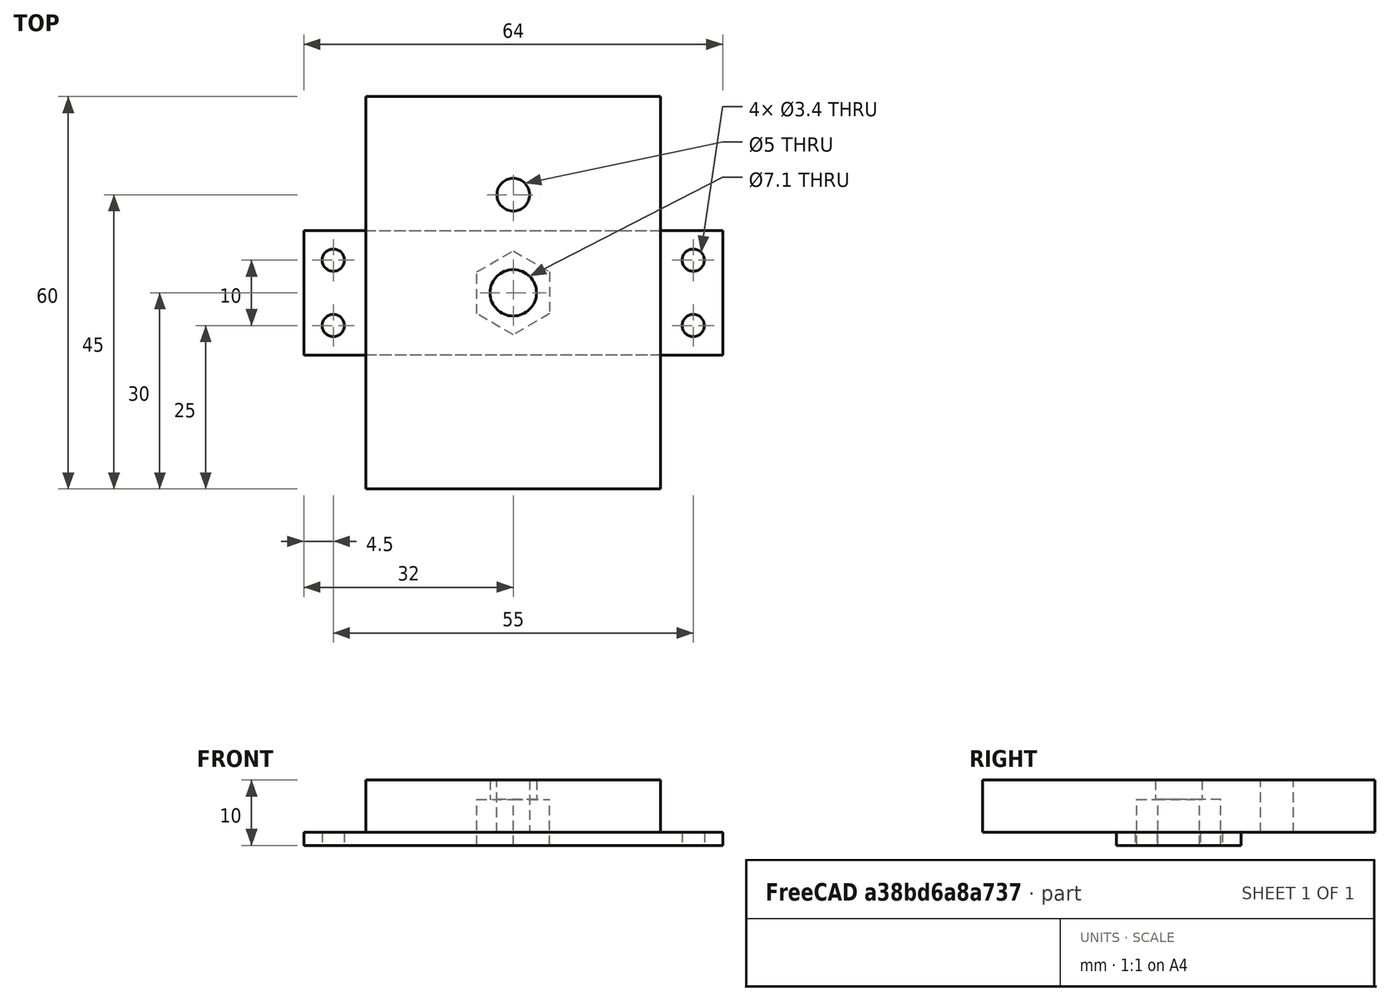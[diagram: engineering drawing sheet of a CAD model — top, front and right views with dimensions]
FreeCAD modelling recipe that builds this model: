
FCSTD DOCUMENT  (FreeCAD 0.21R33668 +26 (Git))
Label: Tripod_Connector
License: All rights reserved
LicenseURL: https://en.wikipedia.org/wiki/All_rights_reserved
objects: Sketcher::SketchObject×6, PartDesign::Pad×2, PartDesign::Hole×2, PartDesign::Pocket×2, Spreadsheet::Sheet×1, PartDesign::Body×1, Mesh::Feature×1
note: 19 computed .brp shape members not serialized (recipe doc carries the construction recipe); baked Part::Feature solids carry a one-line shape summary decoded from their .brp
EXTERNAL_REF file=Casing2.FCStd obj=Spreadsheet

FEATURE [Spreadsheet::Sheet] Spreadsheet
  cells = B2='interface_width; C2(interface_width)==<<Casing2>>#Spreadsheet.interface_width; E2='plate_width; F2(plate_width)==45 mm; H2='hole_rad; I2(hole_rad)==2.5 mm; B3='interface_height; C3(interface_height)==<<Casing2>>#Spreadsheet.beams_width * 2; E3='plate_height; F3(plate_height)==60 mm; H3='dist; I3(dist)==15 mm; B4='interface_depth; C4(interface_depth)==<<Casing2>>#Spreadsheet.walls_thickness; E4='plate_depth; F4(plate_depth)==8 mm; H4='nut_depth; I4(nut_depth)==interface_depth + plate_depth - 3 mm; B5='screw_radius; C5(screw_radius)==<<Casing2>>#Spreadsheet.screw_radius
FEATURE [Sketcher::SketchObject] Sketch
  FullyConstrained = true
  MapMode = 5
  Support = -> [XY_Plane]
  expr: Constraints[10] = Spreadsheet.interface_height - 1 mm
  expr: Constraints[9] = Spreadsheet.interface_width - 1 mm
  sketch-geometry (4):
    g0: LineSegment StartX=-32 StartY=9.5 StartZ=0 EndX=32 EndY=9.5 EndZ=0
    g1: LineSegment StartX=32 StartY=9.5 StartZ=0 EndX=32 EndY=-9.5 EndZ=0
    g2: LineSegment StartX=32 StartY=-9.5 StartZ=0 EndX=-32 EndY=-9.5 EndZ=0
    g3: LineSegment StartX=-32 StartY=-9.5 StartZ=0 EndX=-32 EndY=9.5 EndZ=0
  constraints (11):
    c: Coincident(g0,g1)
    c: Coincident(g1,g2)
    c: Coincident(g2,g3)
    c: Coincident(g3,g0)
    c: Horizontal(g0)
    c: Horizontal(g2)
    c: Vertical(g1)
    c: Vertical(g3)
    c: Symmetric(g0,g2,g-1)
    c: DistanceX(g0,g0) = 64
    c: DistanceY(g3,g3) = 19
FEATURE [PartDesign::Pad] Pad
  Direction = (0,0,1)
  Length = 2
  Length2 = 10
  Profile = -> Sketch
  ReferenceAxis = -> Sketch [N_Axis]
  Type = 0
  expr: Length = Spreadsheet.interface_depth
FEATURE [Sketcher::SketchObject] Sketch001
  FullyConstrained = true
  MapMode = 5
  Placement = pos=(0,0,2) rot=(0,0,1;0rad)
  Support = -> [Pad]
  expr: Constraints[10] = Spreadsheet.interface_height
  expr: Constraints[11] = Spreadsheet.interface_height / 4
  expr: Constraints[12] = Spreadsheet.interface_height / 4
  expr: Constraints[13] = Spreadsheet.interface_height / 4
  expr: Constraints[14] = Spreadsheet.interface_height / 4
  expr: Constraints[15] = Spreadsheet.interface_height / 4
  expr: Constraints[16] = Spreadsheet.interface_height / 4
  expr: Constraints[17] = Spreadsheet.interface_height / 4
  expr: Constraints[18] = Spreadsheet.interface_height / 4
  expr: Constraints[19] = Spreadsheet.screw_radius
  expr: Constraints[20] = Spreadsheet.screw_radius
  expr: Constraints[21] = Spreadsheet.screw_radius
  expr: Constraints[22] = Spreadsheet.screw_radius
  expr: Constraints[9] = Spreadsheet.interface_width
  sketch-geometry (8):
    g0: LineSegment StartX=-32.5 StartY=10 StartZ=0 EndX=32.5 EndY=10 EndZ=0
    g1: LineSegment StartX=32.5 StartY=10 StartZ=0 EndX=32.5 EndY=-10 EndZ=0
    g2: LineSegment StartX=32.5 StartY=-10 StartZ=0 EndX=-32.5 EndY=-10 EndZ=0
    g3: LineSegment StartX=-32.5 StartY=-10 StartZ=0 EndX=-32.5 EndY=10 EndZ=0
    g4: Circle CenterX=-27.5 CenterY=5 CenterZ=0 NormalX=0 NormalY=0 NormalZ=1 AngleXU=0 Radius=1.5
    g5: Circle CenterX=-27.5 CenterY=-5 CenterZ=0 NormalX=0 NormalY=0 NormalZ=1 AngleXU=0 Radius=1.5
    g6: Circle CenterX=27.5 CenterY=5 CenterZ=0 NormalX=0 NormalY=0 NormalZ=1 AngleXU=0 Radius=1.5
    g7: Circle CenterX=27.5 CenterY=-5 CenterZ=0 NormalX=0 NormalY=0 NormalZ=1 AngleXU=0 Radius=1.5
  constraints (23):
    c: Coincident(g0,g1)
    c: Coincident(g1,g2)
    c: Coincident(g2,g3)
    c: Coincident(g3,g0)
    c: Horizontal(g0)
    c: Horizontal(g2)
    c: Vertical(g1)
    c: Vertical(g3)
    c: Symmetric(g0,g2,g-1)
    c: DistanceX(g0,g0) = 65
    c: DistanceY(g3,g3) = 20
    c: DistanceX(g0,g4) = 5
    c: DistanceX(g6,g0) = 5
    c: DistanceX(g7,g1) = 5
    c: DistanceX(g2,g5) = 5
    c: DistanceY(g4,g0) = 5
    c: DistanceY(g6,g0) = 5
    c: DistanceY(g1,g7) = 5
    c: DistanceY(g2,g5) = 5
    c: Radius(g6) = 1.5
    c: Radius(g7) = 1.5
    c: Radius(g4) = 1.5
    c: Radius(g5) = 1.5
FEATURE [PartDesign::Hole] Hole
  BaseFeature = -> Pad
  CustomThreadClearance = 0
  Depth = 134.917
  DepthType = 1
  Diameter = 3.4
  DrillForDepth = false
  DrillPoint = 1
  DrillPointAngle = 118
  HoleCutCountersinkAngle = 90
  HoleCutCustomValues = false
  HoleCutDepth = 0
  HoleCutDiameter = 6.1
  HoleCutType = 0
  ModelThread = false
  Profile = -> Sketch001
  Tapered = false
  TaperedAngle = 90
  ThreadClass = 0
  ThreadDepth = 134.917
  ThreadDepthType = 0
  ThreadDirection = 0
  ThreadFit = 0
  ThreadSize = 9
  ThreadType = 1
  Threaded = false
  UseCustomThreadClearance = false
FEATURE [Sketcher::SketchObject] Sketch002
  FullyConstrained = true
  MapMode = 5
  Placement = pos=(0,0,2) rot=(0,0,1;0rad)
  Support = -> [Hole]
  expr: Constraints[10] = Spreadsheet.plate_height
  expr: Constraints[9] = Spreadsheet.plate_width
  sketch-geometry (4):
    g0: LineSegment StartX=-22.5 StartY=30 StartZ=0 EndX=22.5 EndY=30 EndZ=0
    g1: LineSegment StartX=22.5 StartY=30 StartZ=0 EndX=22.5 EndY=-30 EndZ=0
    g2: LineSegment StartX=22.5 StartY=-30 StartZ=0 EndX=-22.5 EndY=-30 EndZ=0
    g3: LineSegment StartX=-22.5 StartY=-30 StartZ=0 EndX=-22.5 EndY=30 EndZ=0
  constraints (11):
    c: Coincident(g0,g1)
    c: Coincident(g1,g2)
    c: Coincident(g2,g3)
    c: Coincident(g3,g0)
    c: Horizontal(g0)
    c: Horizontal(g2)
    c: Vertical(g1)
    c: Vertical(g3)
    c: Symmetric(g0,g2,g-1)
    c: DistanceX(g0,g0) = 45
    c: DistanceY(g3,g3) = 60
FEATURE [PartDesign::Pad] Pad001
  BaseFeature = -> Hole
  Direction = (0,0,1)
  Length = 8
  Length2 = 10
  Profile = -> Sketch002
  ReferenceAxis = -> Sketch002 [N_Axis]
  Type = 0
  expr: Length = Spreadsheet.plate_depth
FEATURE [Sketcher::SketchObject] Sketch003
  FullyConstrained = true
  MapMode = 5
  Placement = pos=(0,0,10) rot=(0,0,1;0rad)
  Support = -> [Pad001]
  expr: Constraints[1] = Spreadsheet.dist
  expr: Constraints[2] = Spreadsheet.hole_rad
  sketch-geometry (1):
    g0: Circle CenterX=0 CenterY=15 CenterZ=0 NormalX=0 NormalY=0 NormalZ=1 AngleXU=0 Radius=2.5
  constraints (3):
    c: PointOnObject(g0,g-2)
    c: DistanceY(g-1,g0) = 15
    c: Radius(g0) = 2.5
FEATURE [PartDesign::Pocket] Pocket
  BaseFeature = -> Pad001
  Direction = (0,0,-1)
  Length = 5
  Length2 = 5
  Profile = -> Sketch003
  ReferenceAxis = -> Sketch003 [N_Axis]
  Type = 1
FEATURE [Sketcher::SketchObject] Sketch004
  FullyConstrained = true
  MapMode = 5
  Placement = pos=(0,0,10) rot=(0,0,1;0rad)
  Support = -> [Pocket]
  sketch-geometry (1):
    g0: Circle CenterX=0 CenterY=0 CenterZ=0 NormalX=0 NormalY=0 NormalZ=1 AngleXU=0 Radius=2.5
  constraints (2):
    c: Coincident(g0,g-1)
    c: Radius(g0) = 2.5
FEATURE [PartDesign::Hole] Hole001
  BaseFeature = -> Pocket
  CustomThreadClearance = 0
  Depth = 178.356
  DepthType = 1
  Diameter = 7.1
  DrillForDepth = false
  DrillPoint = 1
  DrillPointAngle = 118
  HoleCutCountersinkAngle = 90
  HoleCutCustomValues = false
  HoleCutDepth = 0
  HoleCutDiameter = 8.8
  HoleCutType = 0
  ModelThread = false
  Profile = -> Sketch004
  Tapered = false
  TaperedAngle = 90
  ThreadClass = 0
  ThreadDepth = 178.356
  ThreadDepthType = 0
  ThreadDirection = 0
  ThreadFit = 0
  ThreadSize = 9
  ThreadType = 3
  Threaded = false
  UseCustomThreadClearance = false
FEATURE [Sketcher::SketchObject] Sketch005
  FullyConstrained = true
  MapMode = 5
  Placement = pos=(0,0,0) rot=(1,0,0;3.14159rad)
  Support = -> [Hole001]
  sketch-geometry (7):
    g0: LineSegment StartX=5.55 StartY=3.20429 StartZ=0 EndX=-9e-16 EndY=6.40859 EndZ=0
    g1: LineSegment StartX=-9e-16 StartY=6.40859 StartZ=0 EndX=-5.55 EndY=3.20429 EndZ=0
    g2: LineSegment StartX=-5.55 StartY=3.20429 StartZ=0 EndX=-5.55 EndY=-3.20429 EndZ=0
    g3: LineSegment StartX=-5.55 StartY=-3.20429 StartZ=0 EndX=-9e-16 EndY=-6.40859 EndZ=0
    g4: LineSegment StartX=-9e-16 StartY=-6.40859 StartZ=0 EndX=5.55 EndY=-3.20429 EndZ=0
    g5: LineSegment StartX=5.55 StartY=-3.20429 StartZ=0 EndX=5.55 EndY=3.20429 EndZ=0
    g6: Circle CenterX=0 CenterY=0 CenterZ=0 NormalX=0 NormalY=0 NormalZ=1 AngleXU=0 Radius=6.40859
  constraints (16):
    c: Coincident(g0,g1)
    c: Coincident(g1,g2)
    c: Coincident(g2,g3)
    c: Coincident(g3,g4)
    c: Coincident(g4,g5)
    c: Coincident(g5,g0)
    c: Equal(g0, g1-g5) x5
    c: PointOnObject(g0,g6)
    c: PointOnObject(g1,g6)
    c: PointOnObject(g2,g6)
    c: PointOnObject(g3,g6)
    c: PointOnObject(g4,g6)
    c: PointOnObject(g5,g6)
    c: Coincident(g6,g-1)
    c: Vertical(g5)
    c: DistanceX(g2,g4) = 11.1
FEATURE [PartDesign::Pocket] Pocket001
  BaseFeature = -> Hole001
  Direction = (0,0,1)
  Length = 7
  Length2 = 5
  Profile = -> Sketch005
  ReferenceAxis = -> Sketch005 [N_Axis]
  Type = 0
  expr: Length = Spreadsheet.nut_depth
FEATURE [PartDesign::Body] Body  label="Körper"
  Group = -> [Sketch,Pad,Sketch001,Hole,Sketch002,Pad001,Sketch003,Pocket,Sketch004,Hole001,Sketch005,Pocket001]
  Origin = -> Origin
  Tip = -> Pocket001
FEATURE [Mesh::Feature] Mesh  label="Körper (Meshed)"
